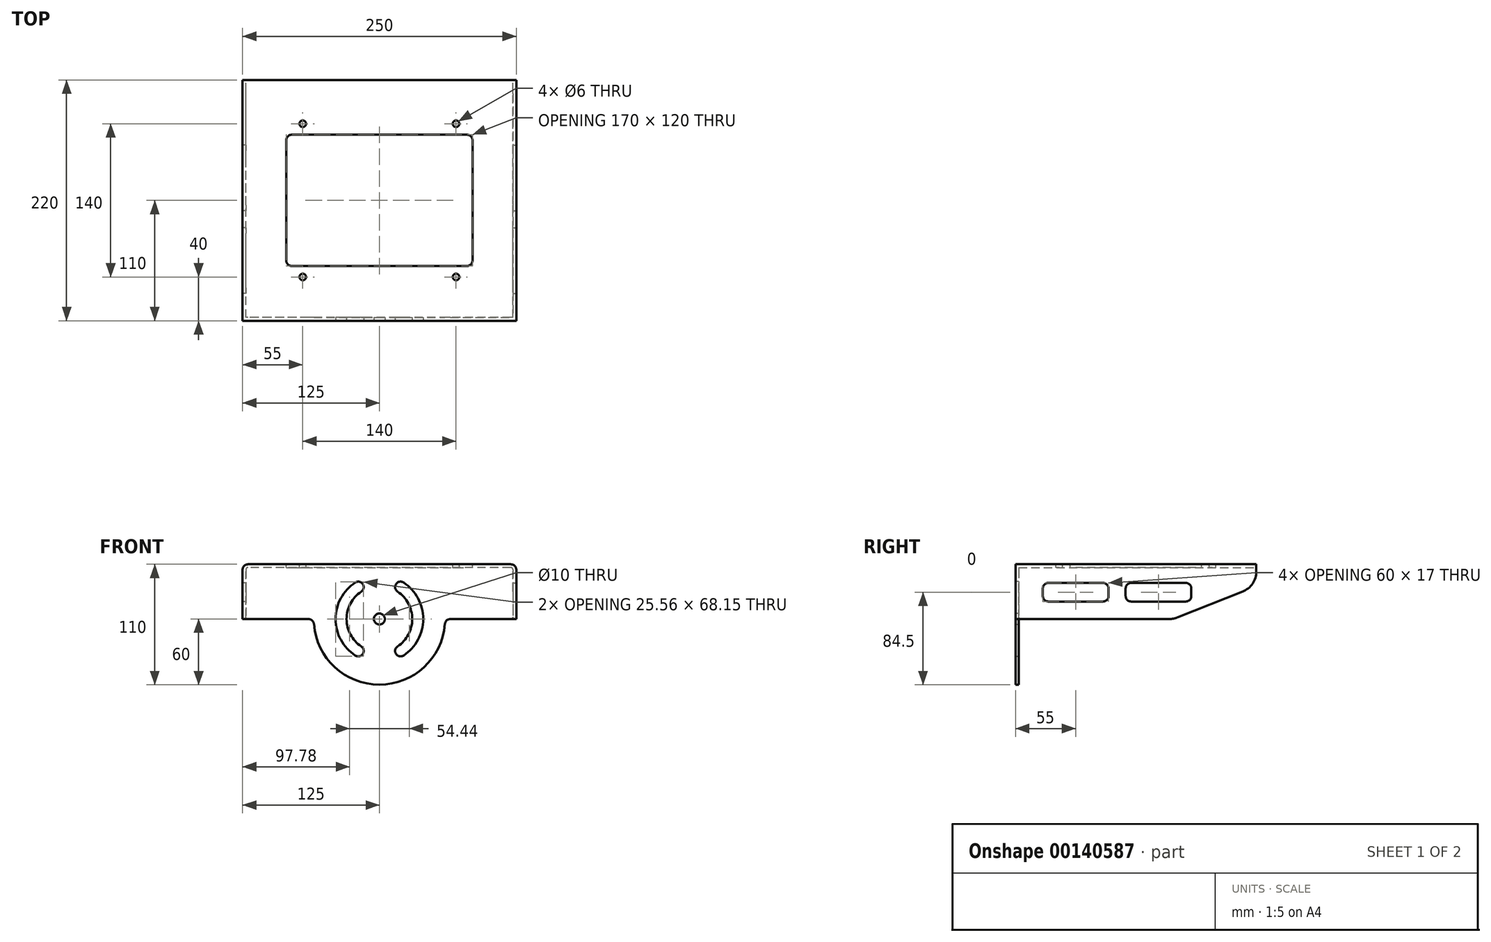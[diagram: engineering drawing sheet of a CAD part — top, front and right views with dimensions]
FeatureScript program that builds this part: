
annotation { "Feature Type Name" : "Feature", "Feature Type Description" : "" }
export const myFeature = defineFeature(function(context is Context, id is Id, definition is map)
    precondition{}
    {
        {
            var Q0;
            Q0=qCreatedBy(makeId("Front.planeOp"),FACE);
            var sketch = newSketch(context, id + "F0", { "sketchPlane" : qUnion([Q0])});
            skArc(sketch, "E0", {"start": v(-59.82, -54.62) * mm, "mid": v(0, -110) * mm, "end": v(59.82, -54.62) * mm});
            skCircle(sketch, "E1", {"center": v(0, -50) * mm, "radius": 5 * mm});
            skLineSegment(sketch, "E2", {"start": v(16.58, -75) * mm, "end": v(16.58, -75) * mm});
            skLineSegment(sketch, "E3", {"start": v(16.58, -25) * mm, "end": v(16.58, -25) * mm});
            skArc(sketch, "E4", {"start": v(16.58, -75) * mm, "mid": v(30, -50) * mm, "end": v(16.58, -25) * mm});
            skArc(sketch, "E5.0", {"start": v(22.11, -83.33) * mm, "mid": v(40, -50) * mm, "end": v(22.11, -16.67) * mm});
            skArc(sketch, "E6", {"start": v(22.11, -16.67) * mm, "mid": v(15.18, -18.07) * mm, "end": v(16.58, -25) * mm});
            skArc(sketch, "E7", {"start": v(22.11, -83.33) * mm, "mid": v(15.18, -81.93) * mm, "end": v(16.58, -75) * mm});
            skArc(sketch, "E8.MirrorCS", {"start": v(-16.58, -75) * mm, "mid": v(-30, -50) * mm, "end": v(-16.58, -25) * mm});
            skArc(sketch, "E9.MirrorCS", {"start": v(-22.11, -16.67) * mm, "mid": v(-15.18, -18.07) * mm, "end": v(-16.58, -25) * mm});
            skArc(sketch, "E10.MirrorCS", {"start": v(-22.11, -83.33) * mm, "mid": v(-40, -50) * mm, "end": v(-22.11, -16.67) * mm});
            skArc(sketch, "E11.MirrorCS", {"start": v(-22.11, -83.33) * mm, "mid": v(-15.18, -81.93) * mm, "end": v(-16.58, -75) * mm});
            skLineSegment(sketch, "E12", {"start": v(125, 0) * mm, "end": v(-125, 0) * mm});
            skPoint(sketch, "E13.visualSharp", {"position": v(-60, -50) * mm});
            skArc(sketch, "E13.filletArc", {"start": v(-59.82, -54.62) * mm, "mid": v(-61.41, -51.33) * mm, "end": v(-64.8, -50) * mm});
            skPoint(sketch, "E14.visualSharp", {"position": v(60, -50) * mm});
            skArc(sketch, "E14.filletArc", {"start": v(64.8, -50) * mm, "mid": v(61.41, -51.33) * mm, "end": v(59.82, -54.62) * mm});
            skPoint(sketch, "E15.visualSharp", {"position": v(-125, -50) * mm});
            skPoint(sketch, "E16.visualSharp", {"position": v(125, -50) * mm});
            skLineSegment(sketch, "E17", {"start": v(-64.8, -50) * mm, "end": v(-125, -50) * mm});
            skLineSegment(sketch, "E18", {"start": v(-125, 0) * mm, "end": v(-125, -50) * mm});
            skLineSegment(sketch, "E19", {"start": v(64.8, -50) * mm, "end": v(125, -50) * mm});
            skLineSegment(sketch, "E20", {"start": v(125, 0) * mm, "end": v(125, -50) * mm});
            skLineSegment(sketch, "E21", {"start": v(-125, 0) * mm, "end": v(-125, 0) * mm});
            skLineSegment(sketch, "E22", {"start": v(-123, 2) * mm, "end": v(125, 2) * mm});
            skLineSegment(sketch, "E23", {"start": v(125, 2) * mm, "end": v(125, 0) * mm});
            skPoint(sketch, "E24.visualSharp", {"position": v(-125, 2) * mm});
            skArc(sketch, "E24.filletArc", {"start": v(-123, 2) * mm, "mid": v(-124.41, 1.41) * mm, "end": v(-125, 0) * mm});
            skSolve(sketch);
        }
        {
            var Q0;
            Q0=qCreatedBy(makeId("Right.planeOp"),FACE);
            cPlane(context, id + "F1", {"entities" : qUnion([Q0]), "cplaneType" : CPlaneType.OFFSET, "offset" : 125 * mm, "width" : 150 * mm, "height" : 150 * mm});
        }
        {
            var Q0;
            Q0=qCreatedBy(id+"F1.planeOp",FACE);
            var sketch = newSketch(context, id + "F2", { "sketchPlane" : qUnion([Q0])});
            skLineSegment(sketch, "E25", {"start": v(0, 0) * mm, "end": v(220, 0) * mm});
            skLineSegment(sketch, "E26", {"start": v(140.74, -50) * mm, "end": v(0, -50) * mm});
            skLineSegment(sketch, "E27", {"start": v(0, -50) * mm, "end": v(0, 0) * mm});
            skLineSegment(sketch, "E28", {"start": v(220, 0) * mm, "end": v(220, -6.43) * mm});
            skLineSegment(sketch, "E29", {"start": v(207.4, -25.01) * mm, "end": v(148.13, -48.58) * mm});
            skPoint(sketch, "E30.visualSharp", {"position": v(220, -20) * mm});
            skArc(sketch, "E30.filletArc", {"start": v(207.4, -25.01) * mm, "mid": v(216.55, -17.66) * mm, "end": v(220, -6.43) * mm});
            skPoint(sketch, "E31.visualSharp", {"position": v(144.57, -50) * mm});
            skArc(sketch, "E31.filletArc", {"start": v(140.74, -50) * mm, "mid": v(144.5, -49.64) * mm, "end": v(148.13, -48.58) * mm});
            skLineSegment(sketch, "E32.bottom", {"start": v(30, -17) * mm, "end": v(80, -17) * mm});
            skLineSegment(sketch, "E32.top", {"start": v(30, -34) * mm, "end": v(80, -34) * mm});
            skLineSegment(sketch, "E32.left", {"start": v(25, -22) * mm, "end": v(25, -29) * mm});
            skLineSegment(sketch, "E32.right", {"start": v(85, -22) * mm, "end": v(85, -29) * mm});
            skPoint(sketch, "E33.visualSharp", {"position": v(85, -17) * mm});
            skArc(sketch, "E33.filletArc", {"start": v(85, -22) * mm, "mid": v(83.54, -18.46) * mm, "end": v(80, -17) * mm});
            skPoint(sketch, "E34.visualSharp", {"position": v(85, -34) * mm});
            skArc(sketch, "E34.filletArc", {"start": v(80, -34) * mm, "mid": v(83.54, -32.54) * mm, "end": v(85, -29) * mm});
            skPoint(sketch, "E35.visualSharp", {"position": v(25, -34) * mm});
            skArc(sketch, "E35.filletArc", {"start": v(25, -29) * mm, "mid": v(26.46, -32.54) * mm, "end": v(30, -34) * mm});
            skPoint(sketch, "E36.visualSharp", {"position": v(25, -17) * mm});
            skArc(sketch, "E36.filletArc", {"start": v(30, -17) * mm, "mid": v(26.46, -18.46) * mm, "end": v(25, -22) * mm});
            skLineSegment(sketch, "E37", {"start": v(105.63, -17) * mm, "end": v(155.63, -17) * mm});
            skLineSegment(sketch, "E38", {"start": v(160.63, -22) * mm, "end": v(160.63, -29) * mm});
            skLineSegment(sketch, "E39", {"start": v(155.63, -34) * mm, "end": v(105.63, -34) * mm});
            skLineSegment(sketch, "E40", {"start": v(100.63, -29) * mm, "end": v(100.63, -22) * mm});
            skPoint(sketch, "E41.visualSharp", {"position": v(100.63, -17) * mm});
            skArc(sketch, "E41.filletArc", {"start": v(105.63, -17) * mm, "mid": v(102.1, -18.46) * mm, "end": v(100.63, -22) * mm});
            skPoint(sketch, "E42.visualSharp", {"position": v(100.63, -34) * mm});
            skArc(sketch, "E42.filletArc", {"start": v(100.63, -29) * mm, "mid": v(102.1, -32.54) * mm, "end": v(105.63, -34) * mm});
            skPoint(sketch, "E43.visualSharp", {"position": v(160.63, -34) * mm});
            skArc(sketch, "E43.filletArc", {"start": v(155.63, -34) * mm, "mid": v(159.16, -32.54) * mm, "end": v(160.63, -29) * mm});
            skPoint(sketch, "E44.visualSharp", {"position": v(160.63, -17) * mm});
            skArc(sketch, "E44.filletArc", {"start": v(160.63, -22) * mm, "mid": v(159.16, -18.46) * mm, "end": v(155.63, -17) * mm});
            skSolve(sketch);
        }
        {
            var Q0;
            Q0=qCreatedBy(makeId("Front.planeOp"),FACE);
            cPlane(context, id + "F3", {"entities" : qUnion([Q0]), "cplaneType" : CPlaneType.OFFSET, "offset" : 220 * mm, "oppositeDirection" : true, "width" : 150 * mm, "height" : 150 * mm});
        }
        {
            var Q0;
            Q0=qCreatedBy(id+"F3.planeOp",FACE);
            var sketch = newSketch(context, id + "F4", { "sketchPlane" : qUnion([Q0])});
            skLineSegment(sketch, "E45.0", {"start": v(125, -2) * mm, "end": v(125, -6.43) * mm});
            skLineSegment(sketch, "E46", {"start": v(123, 0) * mm, "end": v(-123, 0) * mm});
            skLineSegment(sketch, "E47.MirrorCS", {"start": v(-125, -2) * mm, "end": v(-125, -6.43) * mm});
            skPoint(sketch, "E48.visualSharp", {"position": v(125, 0) * mm});
            skArc(sketch, "E48.filletArc", {"start": v(125, -2) * mm, "mid": v(124.41, -0.59) * mm, "end": v(123, 0) * mm});
            skPoint(sketch, "E49.visualSharp", {"position": v(-125, 0) * mm});
            skArc(sketch, "E49.filletArc", {"start": v(-123, 0) * mm, "mid": v(-124.41, -0.59) * mm, "end": v(-125, -2) * mm});
            skLineSegment(sketch, "E50.0", {"start": v(-122, -5) * mm, "end": v(-122, -6.43) * mm});
            skLineSegment(sketch, "E50.1", {"start": v(120, -3) * mm, "end": v(-120, -3) * mm});
            skLineSegment(sketch, "E50.2", {"start": v(122, -5) * mm, "end": v(122, -6.43) * mm});
            skPoint(sketch, "E51.visualSharp", {"position": v(122, -3) * mm});
            skArc(sketch, "E51.filletArc", {"start": v(122, -5) * mm, "mid": v(121.41, -3.59) * mm, "end": v(120, -3) * mm});
            skPoint(sketch, "E52.visualSharp", {"position": v(-122, -3) * mm});
            skArc(sketch, "E52.filletArc", {"start": v(-120, -3) * mm, "mid": v(-121.41, -3.59) * mm, "end": v(-122, -5) * mm});
            skLineSegment(sketch, "E53", {"start": v(-125, -6.43) * mm, "end": v(-122, -6.43) * mm});
            skLineSegment(sketch, "E54", {"start": v(122, -6.43) * mm, "end": v(125, -6.43) * mm});
            skSolve(sketch);
        }
        {
            var Q0;
            Q0=qCreatedBy(makeId("Right.planeOp"),FACE);
            cPlane(context, id + "F5", {"entities" : qUnion([Q0]), "cplaneType" : CPlaneType.OFFSET, "offset" : 125 * mm, "oppositeDirection" : true, "width" : 150 * mm, "height" : 150 * mm});
        }
        {
            var Q0;
            Q0=qCreatedBy(id+"F5.planeOp",FACE);
            var sketch = newSketch(context, id + "F6", { "sketchPlane" : qUnion([Q0])});
            skLineSegment(sketch, "E55.0.0", {"start": v(220, 0) * mm, "end": v(0, 0) * mm});
            skLineSegment(sketch, "E55.0.1", {"start": v(0, 0) * mm, "end": v(0, -50) * mm});
            skLineSegment(sketch, "E55.0.2", {"start": v(0, -50) * mm, "end": v(140.74, -50) * mm});
            skArc(sketch, "E55.0.3", {"start": v(140.74, -50) * mm, "mid": v(144.5, -49.64) * mm, "end": v(148.13, -48.58) * mm});
            skLineSegment(sketch, "E55.0.4", {"start": v(148.13, -48.58) * mm, "end": v(207.4, -25.01) * mm});
            skArc(sketch, "E55.0.5", {"start": v(207.4, -25.01) * mm, "mid": v(216.55, -17.66) * mm, "end": v(220, -6.43) * mm});
            skLineSegment(sketch, "E55.0.6", {"start": v(220, -6.43) * mm, "end": v(220, 0) * mm});
            skLineSegment(sketch, "E56.0", {"start": v(30, -17) * mm, "end": v(80, -17) * mm});
            skArc(sketch, "E57.0", {"start": v(85, -22) * mm, "mid": v(83.54, -18.46) * mm, "end": v(80, -17) * mm});
            skLineSegment(sketch, "E58.0", {"start": v(85, -22) * mm, "end": v(85, -29) * mm});
            skPoint(sketch, "E59.0", {"position": v(85, -34) * mm});
            skArc(sketch, "E60.0", {"start": v(80, -34) * mm, "mid": v(83.54, -32.54) * mm, "end": v(85, -29) * mm});
            skLineSegment(sketch, "E61.0", {"start": v(30, -34) * mm, "end": v(80, -34) * mm});
            skArc(sketch, "E62.0", {"start": v(25, -29) * mm, "mid": v(26.46, -32.54) * mm, "end": v(30, -34) * mm});
            skLineSegment(sketch, "E63.0", {"start": v(25, -22) * mm, "end": v(25, -29) * mm});
            skArc(sketch, "E64.0", {"start": v(30, -17) * mm, "mid": v(26.46, -18.46) * mm, "end": v(25, -22) * mm});
            skArc(sketch, "E65.0", {"start": v(105.63, -17) * mm, "mid": v(102.1, -18.46) * mm, "end": v(100.63, -22) * mm});
            skLineSegment(sketch, "E65.1", {"start": v(100.63, -29) * mm, "end": v(100.63, -22) * mm});
            skArc(sketch, "E65.2", {"start": v(100.63, -29) * mm, "mid": v(102.1, -32.54) * mm, "end": v(105.63, -34) * mm});
            skLineSegment(sketch, "E65.3", {"start": v(155.63, -34) * mm, "end": v(105.63, -34) * mm});
            skArc(sketch, "E65.4", {"start": v(155.63, -34) * mm, "mid": v(159.16, -32.54) * mm, "end": v(160.63, -29) * mm});
            skLineSegment(sketch, "E65.5", {"start": v(160.63, -22) * mm, "end": v(160.63, -29) * mm});
            skArc(sketch, "E65.6", {"start": v(160.63, -22) * mm, "mid": v(159.16, -18.46) * mm, "end": v(155.63, -17) * mm});
            skLineSegment(sketch, "E65.7", {"start": v(105.63, -17) * mm, "end": v(155.63, -17) * mm});
            skSolve(sketch);
        }
        {
            var Q0;
            Q0=makeQuery(id+"F4.imprint","IMPRINT",FACE,{"disambiguationData":[TD([[makeQuery(id+"F4.imprint","IMPRINT",EDGE,{"derivedFrom":sQuery(id+"F4.wireOp",EDGE,"E45.0")}),-1.0]])]});
            extrude(context, id + "F7", {"entities" : qUnion([Q0]), "depth" : 220 * mm});
        }
        {
            var Q0;
            Q0 = qSketchRegion(id + "F6", true);
            extrude(context, id + "F8", {"entities" : qUnion([Q0]), "operationType" : NewBodyOperationType.ADD, "depth" : 3 * mm});
        }
        {
            var Q0;
            Q0=makeQuery(id+"F2.imprint","IMPRINT",FACE,{"disambiguationData":[TD([[makeQuery(id+"F2.imprint","IMPRINT",EDGE,{"derivedFrom":sQuery(id+"F2.wireOp",EDGE,"E25")}),-1.0]])]});
            extrude(context, id + "F9", {"entities" : qUnion([Q0]), "operationType" : NewBodyOperationType.ADD, "oppositeDirection" : true, "depth" : 3 * mm});
        }
        {
            var Q0;
            Q0=makeQuery(id+"F0.imprint","IMPRINT",FACE,{"disambiguationData":[TD([[makeQuery(id+"F0.imprint","IMPRINT",EDGE,{"derivedFrom":sQuery(id+"F0.wireOp",EDGE,"E0")}),1.0]])]});
            extrude(context, id + "F10", {"entities" : qUnion([Q0]), "operationType" : NewBodyOperationType.ADD, "oppositeDirection" : true, "depth" : 3 * mm});
        }
        {
            var Q0;
            Q0=makeQuery(id+"F9.opExtrude","CAP_EDGE",EDGE,{"disambiguationData":[OSD([sQuery(id+"F2.wireOp",EDGE,"E25")])],"isStart":true});
            fillet(context, id + "F11", {"entities" : qUnion([Q0]), "radius" : 5 * mm, "tangentPropagation" : true, "allowEdgeOverflow" : false});
        }
        {
            var Q0;
            Q0=makeQuery(id+"F8.opExtrude","CAP_EDGE",EDGE,{"disambiguationData":[OSD([sQuery(id+"F6.wireOp",EDGE,"E55.0.0")])],"isStart":true});
            fillet(context, id + "F12", {"entities" : qUnion([Q0]), "radius" : 5 * mm, "tangentPropagation" : true, "allowEdgeOverflow" : false});
        }
        {
            var Q0;
            Q0=makeQuery(id+"F9.boolean.opBoolean","MERGE",FACE,{"derivedFrom":[makeQuery(id+"F8.boolean.opBoolean","MERGE",FACE,{"derivedFrom":[makeQuery(id+"F7.opExtrude","SWEPT_FACE",FACE,{"disambiguationData":[OSD([sQuery(id+"F4.wireOp",EDGE,"E46")])]}),makeQuery(id+"F8.opExtrude","SWEPT_FACE",FACE,{"disambiguationData":[OSD([sQuery(id+"F6.wireOp",EDGE,"E55.0.0")])]})]}),makeQuery(id+"F9.opExtrude","SWEPT_FACE",FACE,{"disambiguationData":[OSD([sQuery(id+"F2.wireOp",EDGE,"E25")])]})]});
            var sketch = newSketch(context, id + "F13", { "sketchPlane" : qUnion([Q0])});
            skLineSegment(sketch, "E66.1", {"start": v(120, 220) * mm, "end": v(-120, 220) * mm});
            skLineSegment(sketch, "E66.2", {"start": v(-120, 220) * mm, "end": v(-120, 0) * mm});
            skLineSegment(sketch, "E66.3", {"start": v(120, 0) * mm, "end": v(120, 220) * mm});
            skLineSegment(sketch, "E66.4", {"start": v(120, 0) * mm, "end": v(-120, 0) * mm});
            skLineSegment(sketch, "E67.bottom", {"start": v(80, 50) * mm, "end": v(-80, 50) * mm});
            skLineSegment(sketch, "E67.top", {"start": v(80, 170) * mm, "end": v(-80, 170) * mm});
            skLineSegment(sketch, "E67.left", {"start": v(85, 55) * mm, "end": v(85, 165) * mm});
            skLineSegment(sketch, "E67.right", {"start": v(-85, 55) * mm, "end": v(-85, 165) * mm});
            skPoint(sketch, "E67.middle", {"position": v(0, 110) * mm});
            skPoint(sketch, "E67.middle.positionSnap0", {"position": v(120, 110) * mm});
            skPoint(sketch, "E67.centerSnap0", {"position": v(120, 110) * mm});
            skPoint(sketch, "E68.visualSharp", {"position": v(-85, 170) * mm});
            skArc(sketch, "E68.filletArc", {"start": v(-80, 170) * mm, "mid": v(-83.54, 168.54) * mm, "end": v(-85, 165) * mm});
            skPoint(sketch, "E69.visualSharp", {"position": v(-85, 50) * mm});
            skArc(sketch, "E69.filletArc", {"start": v(-85, 55) * mm, "mid": v(-83.54, 51.46) * mm, "end": v(-80, 50) * mm});
            skPoint(sketch, "E70.visualSharp", {"position": v(85, 50) * mm});
            skArc(sketch, "E70.filletArc", {"start": v(80, 50) * mm, "mid": v(83.54, 51.46) * mm, "end": v(85, 55) * mm});
            skPoint(sketch, "E71.visualSharp", {"position": v(85, 170) * mm});
            skArc(sketch, "E71.filletArc", {"start": v(85, 165) * mm, "mid": v(83.54, 168.54) * mm, "end": v(80, 170) * mm});
            skLineSegment(sketch, "E72.bottom", {"start": v(70, 40) * mm, "end": v(-70, 40) * mm, "construction": true});
            skLineSegment(sketch, "E72.top", {"start": v(70, 180) * mm, "end": v(-70, 180) * mm, "construction": true});
            skLineSegment(sketch, "E72.left", {"start": v(70, 40) * mm, "end": v(70, 180) * mm, "construction": true});
            skLineSegment(sketch, "E72.right", {"start": v(-70, 40) * mm, "end": v(-70, 180) * mm, "construction": true});
            skCircle(sketch, "E73", {"center": v(-70, 180) * mm, "radius": 3 * mm});
            skCircle(sketch, "E74", {"center": v(-70, 40) * mm, "radius": 3 * mm});
            skCircle(sketch, "E75", {"center": v(70, 40) * mm, "radius": 3 * mm});
            skCircle(sketch, "E76", {"center": v(70, 180) * mm, "radius": 3 * mm});
            skSolve(sketch);
        }
        {
            var Q0;
            Q0=makeQuery(id+"F13.imprint","IMPRINT",FACE,{"disambiguationData":[TD([[makeQuery(id+"F13.imprint","IMPRINT",EDGE,{"derivedFrom":sQuery(id+"F13.wireOp",EDGE,"E67.bottom")}),-1.0]])]});
            var Q1;
            Q1=makeQuery(id+"F13.imprint","IMPRINT",FACE,{"disambiguationData":[TD([[makeQuery(id+"F13.imprint","IMPRINT",EDGE,{"derivedFrom":sQuery(id+"F13.wireOp",EDGE,"E73")}),1.0]])]});
            var Q2;
            Q2=makeQuery(id+"F13.imprint","IMPRINT",FACE,{"disambiguationData":[TD([[makeQuery(id+"F13.imprint","IMPRINT",EDGE,{"derivedFrom":sQuery(id+"F13.wireOp",EDGE,"E74")}),1.0]])]});
            var Q3;
            Q3=makeQuery(id+"F13.imprint","IMPRINT",FACE,{"disambiguationData":[TD([[makeQuery(id+"F13.imprint","IMPRINT",EDGE,{"derivedFrom":sQuery(id+"F13.wireOp",EDGE,"E75")}),1.0]])]});
            var Q4;
            Q4=makeQuery(id+"F13.imprint","IMPRINT",FACE,{"disambiguationData":[TD([[makeQuery(id+"F13.imprint","IMPRINT",EDGE,{"derivedFrom":sQuery(id+"F13.wireOp",EDGE,"E76")}),1.0]])]});
            extrude(context, id + "F14", {"entities" : qUnion([Q0, Q1, Q2, Q3, Q4]), "operationType" : NewBodyOperationType.REMOVE, "oppositeDirection" : true, "depth" : 25 * mm});
        }
    });
